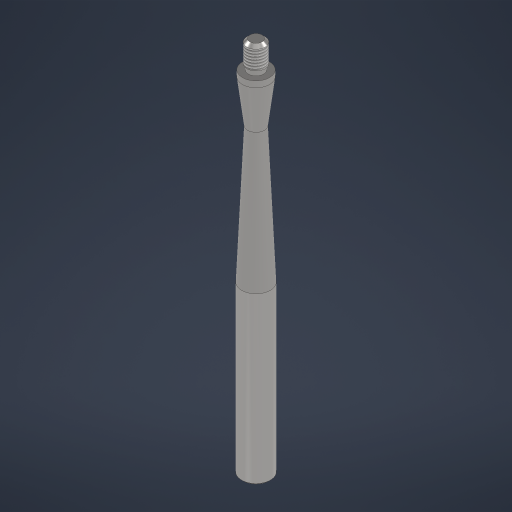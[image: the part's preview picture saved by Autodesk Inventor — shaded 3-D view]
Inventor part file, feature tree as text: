
AUTODESK INVENTOR PART (.ipt)
format: ipt  version: 2024.3 (Build 283343000, 343)  size: 230,400 bytes
history: native  units: mm
features: chamfer x2, sketch x2, revolve x1, thread x1, hole x1, other x1
ambient origin geometry x8: Origin, YZ Plane, XZ Plane, XY Plane, X Axis, Y Axis, Z Axis, Center Point
bodies: Solid1 (feature_tree)
feature tree (8):
  revolve  "Revolution1"  [1 undecoded]
  thread  "Thread1"  [1 undecoded]
  hole  "Hole1"  [1 undecoded]
  chamfer  "Chamfer2"  Distance=3.0mm
  chamfer  "Chamfer3"  Distance=18.0mm
  sketch  "Sketch1"  dims[d0=250.0mm d1=19.0mm d2=110.0mm]
  sketch  "Sketch2"  dims[d5=11.14103mm d6=12.0mm d7=3.0mm d9=18.0mm d10=4.0mm d11=10.0mm d12=60.0deg d13=18.0mm d14=0.436332mm d15=90.0deg d16=1.218746mm d17=200.0mm d18=232.0mm d19=50.0mm d20=14.42265mm d21=13.268mm d22=0.0mm d23=15.0mm d24=0.5mm d25=15.5mm d26=2.0mm d27=90.0deg d28=80.0mm d29=20.594885mm d41=2.0mm d42=2.0mm d43=45.0deg d44=1.0mm d45=2.0mm d46=45.0deg]
  other  "Finish1"
note: 3 required parameter values undecoded (feature->parameter linkage not recoverable at this tier; creation-order binding heuristic only, values carry confidence <= 0.55)